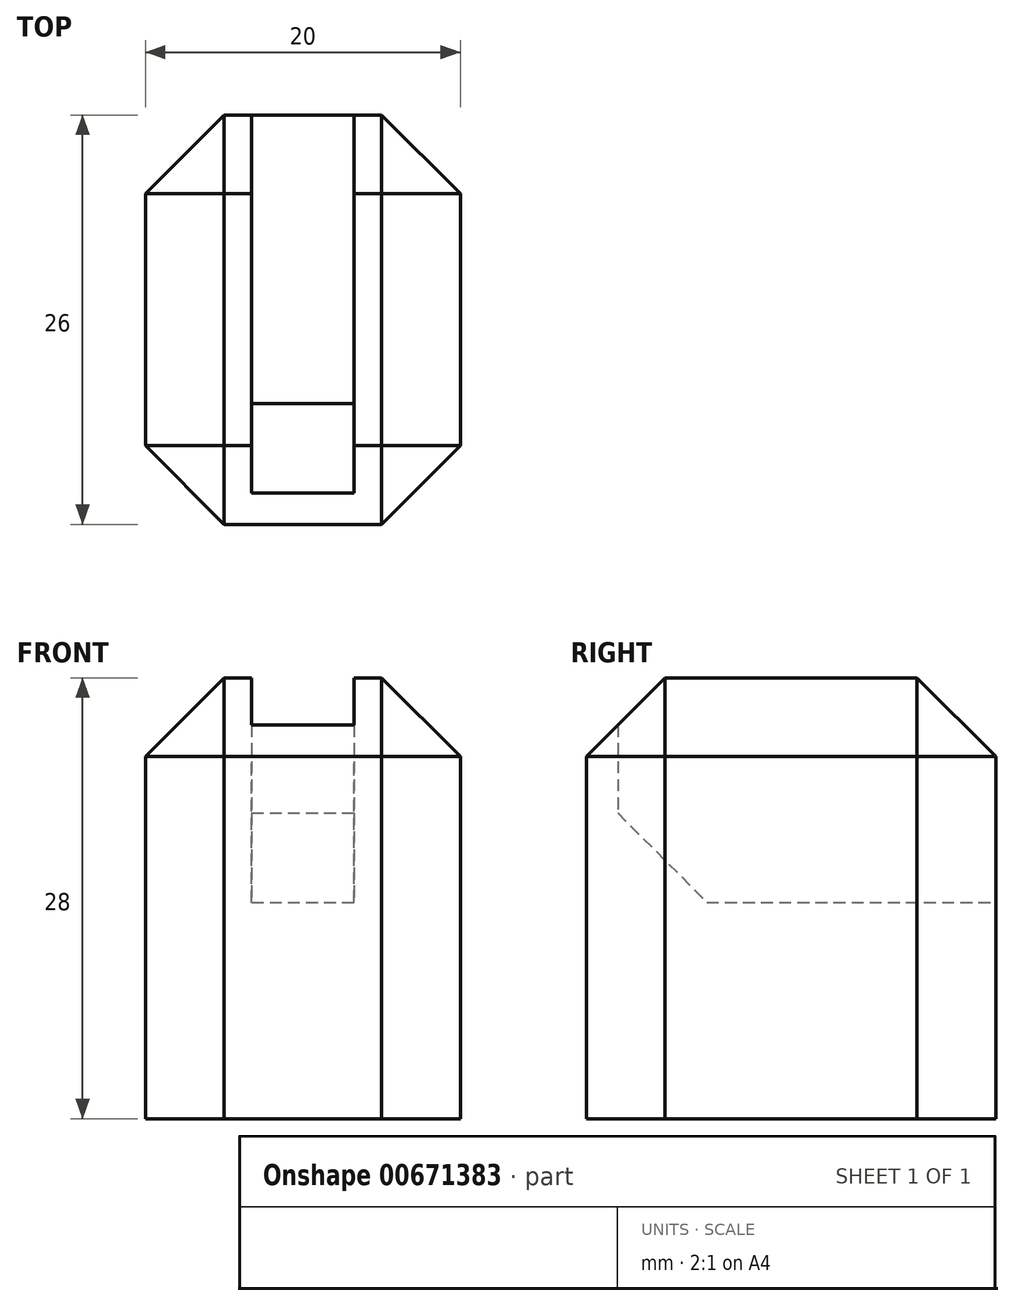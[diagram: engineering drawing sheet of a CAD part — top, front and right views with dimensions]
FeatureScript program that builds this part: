
annotation { "Feature Type Name" : "Feature", "Feature Type Description" : "" }
export const myFeature = defineFeature(function(context is Context, id is Id, definition is map)
    precondition{}
    {
        {
            var Q0;
            Q0=qCreatedBy(makeId("Top.planeOp"),FACE);
            var sketch = newSketch(context, id + "F0", { "sketchPlane" : qUnion([Q0])});
            skLineSegment(sketch, "E0.bottom", {"start": v(10, 13) * mm, "end": v(-10, 13) * mm});
            skLineSegment(sketch, "E0.top", {"start": v(10, -13) * mm, "end": v(-10, -13) * mm});
            skLineSegment(sketch, "E0.left", {"start": v(10, 13) * mm, "end": v(10, -13) * mm});
            skLineSegment(sketch, "E0.right", {"start": v(-10, 13) * mm, "end": v(-10, -13) * mm});
            skPoint(sketch, "E0.middle", {"position": v(0, 0) * mm});
            skSolve(sketch);
        }
        {
            var Q0;
            Q0 = qSketchRegion(id + "F0", true);
            extrude(context, id + "F1", {"entities" : qUnion([Q0]), "depth" : 28 * mm, "offsetDistance" : 25 * mm});
        }
        {
            var Q0;
            Q0=qCreatedBy(makeId("Right.planeOp"),FACE);
            var sketch = newSketch(context, id + "F2", { "sketchPlane" : qUnion([Q0])});
            skLineSegment(sketch, "E1", {"start": v(-11, 28) * mm, "end": v(-11, 19.4) * mm});
            skLineSegment(sketch, "E2", {"start": v(-11, 19.4) * mm, "end": v(-5.34, 13.75) * mm});
            skLineSegment(sketch, "E3", {"start": v(-5.34, 13.75) * mm, "end": v(13, 13.75) * mm});
            skLineSegment(sketch, "E4", {"start": v(13, 13.75) * mm, "end": v(13, 28) * mm});
            skLineSegment(sketch, "E5", {"start": v(13, 28) * mm, "end": v(-11, 28) * mm});
            skSolve(sketch);
        }
        {
            var Q0;
            Q0 = qSketchRegion(id + "F2", true);
            extrude(context, id + "F3", {"entities" : qUnion([Q0]), "operationType" : NewBodyOperationType.REMOVE, "oppositeDirection" : true, "depth" : (6.5 / 2) * mm, "offsetDistance" : 25 * mm, "hasSecondDirection" : true, "secondDirectionOppositeDirection" : false, "secondDirectionDepth" : (6.5 / 2) * mm});
        }
        {
            var Q0;
            Q0=makeQuery(id+"F1.opExtrude","CAP_EDGE",EDGE,{"disambiguationData":[OSD([sQuery(id+"F0.wireOp",EDGE,"E0.left")])],"isStart":false});
            var Q1;
            Q1=makeQuery(id+"F1.opExtrude","CAP_EDGE",EDGE,{"disambiguationData":[OSD([sQuery(id+"F0.wireOp",EDGE,"E0.top")])],"isStart":false});
            var Q2;
            Q2=makeQuery(id+"F1.opExtrude","CAP_EDGE",EDGE,{"disambiguationData":[OSD([sQuery(id+"F0.wireOp",EDGE,"E0.right")])],"isStart":false});
            var Q3;
            Q3=makeQuery(id+"F1.opExtrude","SWEPT_EDGE",EDGE,{"disambiguationData":[OSD([sQuery(id+"F0.wireOp",EDGE,"E0.top"),sQuery(id+"F0.wireOp",EDGE,"E0.left")])]});
            var Q4;
            Q4=makeQuery(id+"F1.opExtrude","SWEPT_EDGE",EDGE,{"disambiguationData":[OSD([sQuery(id+"F0.wireOp",EDGE,"E0.top"),sQuery(id+"F0.wireOp",EDGE,"E0.right")])]});
            var Q5;
            Q5=makeQuery(id+"F1.opExtrude","SWEPT_EDGE",EDGE,{"disambiguationData":[OSD([sQuery(id+"F0.wireOp",EDGE,"E0.bottom"),sQuery(id+"F0.wireOp",EDGE,"E0.left")])]});
            var Q6;
            Q6=makeQuery(id+"F1.opExtrude","SWEPT_EDGE",EDGE,{"disambiguationData":[OSD([sQuery(id+"F0.wireOp",EDGE,"E0.bottom"),sQuery(id+"F0.wireOp",EDGE,"E0.right")])]});
            var Q7;
            {var subQ0=sQuery(id+"F0.wireOp",EDGE,"E0.bottom");var subQ1=sQuery(id+"F0.wireOp",EDGE,"E0.right");Q7=makeQuery(id+"F3.boolean.opBoolean","SPLIT",EDGE,{"disambiguationData":[TD([makeQuery(id+"F1.opExtrude","SWEPT_FACE",FACE,{"disambiguationData":[OSD([subQ1])]})])],"derivedFrom":makeQuery(id+"F1.opExtrude","CAP_EDGE",EDGE,{"disambiguationData":[OSD([subQ0])],"isStart":false})});}
            var Q8;
            {var subQ0=sQuery(id+"F0.wireOp",EDGE,"E0.bottom");var subQ1=sQuery(id+"F0.wireOp",EDGE,"E0.left");Q8=makeQuery(id+"F3.boolean.opBoolean","SPLIT",EDGE,{"disambiguationData":[TD([makeQuery(id+"F1.opExtrude","SWEPT_FACE",FACE,{"disambiguationData":[OSD([subQ1])]})])],"derivedFrom":makeQuery(id+"F1.opExtrude","CAP_EDGE",EDGE,{"disambiguationData":[OSD([subQ0])],"isStart":false})});}
            chamfer(context, id + "F4", {"entities" : qUnion([Q0, Q1, Q2, Q3, Q4, Q5, Q6, Q7, Q8]), "width" : 5 * mm, "tangentPropagation" : true});
        }
    });
